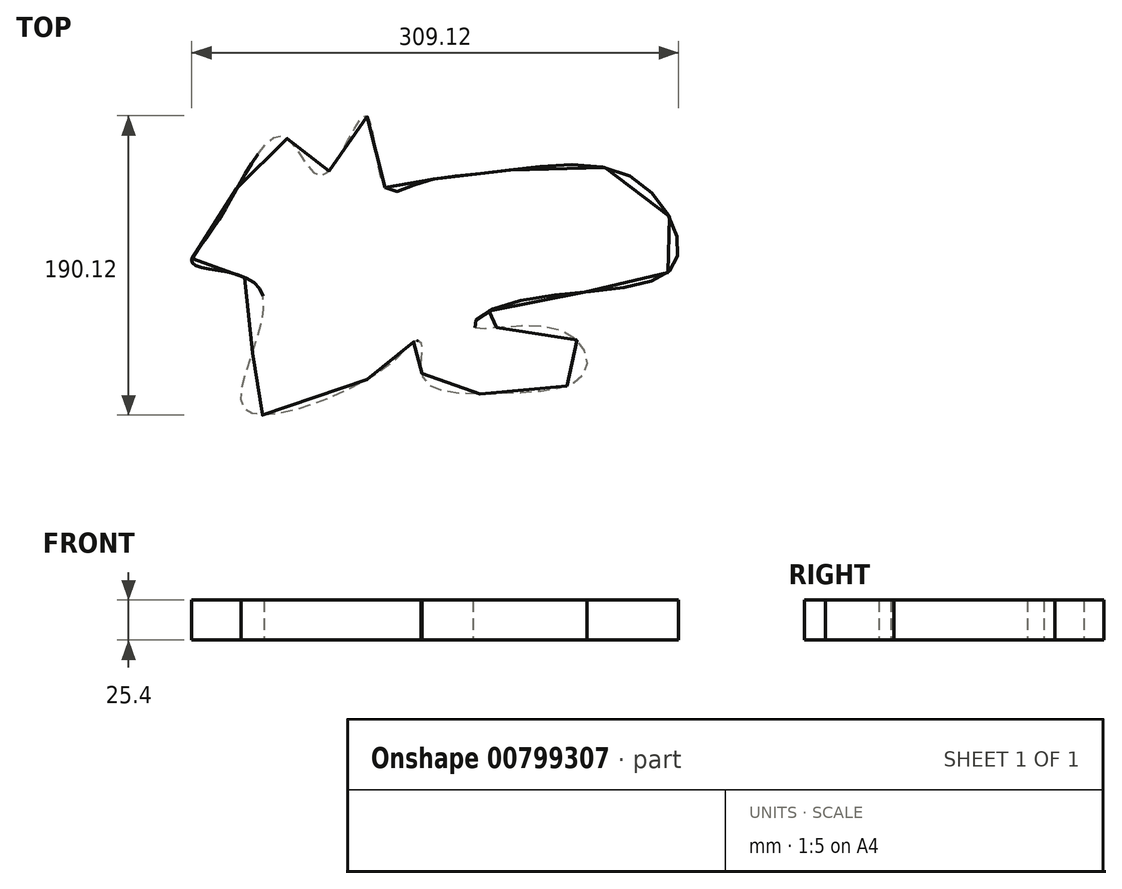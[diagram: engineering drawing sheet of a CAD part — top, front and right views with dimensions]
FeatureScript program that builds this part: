
annotation { "Feature Type Name" : "Feature", "Feature Type Description" : "" }
export const myFeature = defineFeature(function(context is Context, id is Id, definition is map)
    precondition{}
    {
        {
            var Q0;
            Q0=qCreatedBy(makeId("Top.planeOp"),FACE);
            var sketch = newSketch(context, id + "F0", { "sketchPlane" : qUnion([Q0])});
            skFitSpline(sketch, "E0", {"points": [v(-103.65, 37.23) * mm, v(-83.6, 39.46) * mm, v(-33.66, 47.03) * mm, v(50.15, 45.25) * mm, v(82.7, 0) * mm, v(66.65, -22.07) * mm, v(-29.2, -37.67) * mm, v(-47.03, -51.5) * mm, v(8.25, -53.28) * mm, v(22.96, -80.92) * mm, v(-31.43, -93.85) * mm, v(-79.13, -84.04) * mm, v(-80.47, -61.3) * mm, v(-85.37, -60.85) * mm, v(-105.88, -79.13) * mm, v(-193.26, -102.76) * mm, v(-182.12, -28.76) * mm, v(-224.92, -11.81) * mm, v(-212.88, 10.92) * mm, v(-168.3, 69.77) * mm, v(-143.78, 44.8) * mm, v(-116.14, 82.7) * mm, v(-103.65, 37.23) * mm]});
            skSolve(sketch);
        }
        {
            var Q0;
            Q0=makeQuery(id+"F0.imprint","IMPRINT",FACE,{"disambiguationData":[TD([[makeQuery(id+"F0.imprint","IMPRINT",EDGE,{"derivedFrom":sQuery(id+"F0.wireOp",EDGE,"E0")}),-1.0]])]});
            extrude(context, id + "F1", {"entities" : qUnion([Q0]), "depth" : 25.4 * mm, "offsetDistance" : 25.4 * mm});
        }
    });
